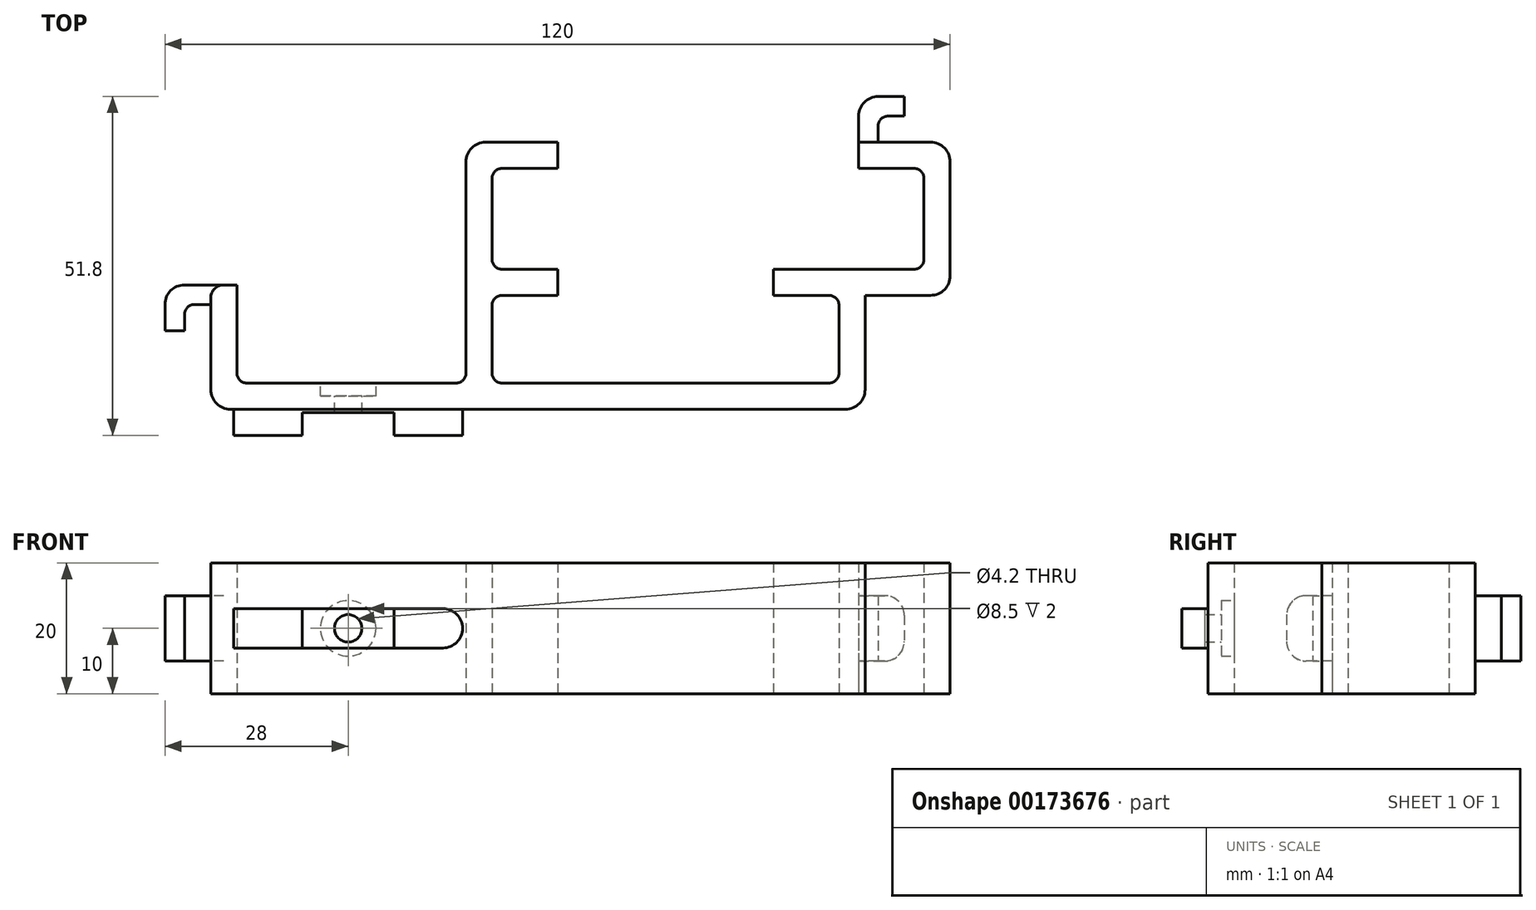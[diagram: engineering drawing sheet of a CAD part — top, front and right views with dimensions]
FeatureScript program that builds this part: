
annotation { "Feature Type Name" : "Feature", "Feature Type Description" : "" }
export const myFeature = defineFeature(function(context is Context, id is Id, definition is map)
    precondition{}
    {
        {
            var Q0;
            Q0=qCreatedBy(makeId("Top.planeOp"),FACE);
            var sketch = newSketch(context, id + "F0", { "sketchPlane" : qUnion([Q0])});
            skLineSegment(sketch, "E0", {"start": v(-35, 0) * mm, "end": v(0, 0) * mm});
            skLineSegment(sketch, "E1", {"start": v(0, 0) * mm, "end": v(0, 36.8) * mm});
            skLineSegment(sketch, "E2", {"start": v(0, 36.8) * mm, "end": v(14, 36.8) * mm});
            skLineSegment(sketch, "E3", {"start": v(14, 36.8) * mm, "end": v(14, 32.8) * mm});
            skLineSegment(sketch, "E4", {"start": v(14, 32.8) * mm, "end": v(4, 32.8) * mm});
            skLineSegment(sketch, "E5", {"start": v(4, 32.8) * mm, "end": v(4, 17.4) * mm});
            skLineSegment(sketch, "E6", {"start": v(4, 17.4) * mm, "end": v(14, 17.4) * mm});
            skLineSegment(sketch, "E7", {"start": v(14, 17.4) * mm, "end": v(14, 13.4) * mm});
            skLineSegment(sketch, "E8", {"start": v(14, 13.4) * mm, "end": v(4, 13.4) * mm});
            skLineSegment(sketch, "E9", {"start": v(4, 13.4) * mm, "end": v(4, 0) * mm});
            skLineSegment(sketch, "E10", {"start": v(4, 0) * mm, "end": v(57, 0) * mm});
            skLineSegment(sketch, "E11", {"start": v(57, 0) * mm, "end": v(57, 13.4) * mm});
            skLineSegment(sketch, "E12", {"start": v(57, 13.4) * mm, "end": v(47, 13.4) * mm});
            skLineSegment(sketch, "E13", {"start": v(47, 13.4) * mm, "end": v(47, 17.4) * mm});
            skLineSegment(sketch, "E14", {"start": v(47, 17.4) * mm, "end": v(70, 17.4) * mm});
            skLineSegment(sketch, "E15", {"start": v(70, 17.4) * mm, "end": v(70, 32.8) * mm});
            skLineSegment(sketch, "E16", {"start": v(70, 32.8) * mm, "end": v(60, 32.8) * mm});
            skLineSegment(sketch, "E17", {"start": v(60, 32.8) * mm, "end": v(60, 36.8) * mm});
            skLineSegment(sketch, "E18", {"start": v(60, 36.8) * mm, "end": v(74, 36.8) * mm});
            skLineSegment(sketch, "E19", {"start": v(74, 36.8) * mm, "end": v(74, 13.4) * mm});
            skLineSegment(sketch, "E20", {"start": v(74, 13.4) * mm, "end": v(61, 13.4) * mm});
            skLineSegment(sketch, "E21", {"start": v(61, 13.4) * mm, "end": v(61, -4) * mm});
            skLineSegment(sketch, "E22", {"start": v(61, -4) * mm, "end": v(-39, -4) * mm});
            skLineSegment(sketch, "E23", {"start": v(-39, -4) * mm, "end": v(-39, 15) * mm});
            skLineSegment(sketch, "E24", {"start": v(-39, 15) * mm, "end": v(-35, 15) * mm});
            skLineSegment(sketch, "E25", {"start": v(-35, 15) * mm, "end": v(-35, 0) * mm});
            skSolve(sketch);
        }
        {
            var Q0;
            Q0 = qSketchRegion(id + "F0", true);
            extrude(context, id + "F1", {"entities" : qUnion([Q0]), "endBound" : BoundingType.SYMMETRIC, "depth" : 20 * mm});
        }
        {
            var Q0;
            Q0=qCreatedBy(makeId("Top.planeOp"),FACE);
            var sketch = newSketch(context, id + "F2", { "sketchPlane" : qUnion([Q0])});
            skLineSegment(sketch, "E26.0", {"start": v(60, 36.8) * mm, "end": v(74, 36.8) * mm});
            skLineSegment(sketch, "E27.0", {"start": v(-39, -4) * mm, "end": v(-39, 15) * mm});
            skLineSegment(sketch, "E28", {"start": v(60, 36.8) * mm, "end": v(60, 43.8) * mm});
            skLineSegment(sketch, "E29", {"start": v(60, 43.8) * mm, "end": v(67, 43.8) * mm});
            skLineSegment(sketch, "E30", {"start": v(67, 43.8) * mm, "end": v(67, 40.8) * mm});
            skLineSegment(sketch, "E31", {"start": v(67, 40.8) * mm, "end": v(63, 40.8) * mm});
            skLineSegment(sketch, "E32", {"start": v(63, 40.8) * mm, "end": v(63, 36.8) * mm});
            skLineSegment(sketch, "E33", {"start": v(63, 36.8) * mm, "end": v(60, 36.8) * mm});
            skLineSegment(sketch, "E34", {"start": v(-39, 15) * mm, "end": v(-46, 15) * mm});
            skLineSegment(sketch, "E35", {"start": v(-46, 15) * mm, "end": v(-46, 8) * mm});
            skLineSegment(sketch, "E36", {"start": v(-46, 8) * mm, "end": v(-43, 8) * mm});
            skLineSegment(sketch, "E37", {"start": v(-43, 8) * mm, "end": v(-43, 12) * mm});
            skLineSegment(sketch, "E38", {"start": v(-43, 12) * mm, "end": v(-39, 12) * mm});
            skLineSegment(sketch, "E39", {"start": v(-39, 12) * mm, "end": v(-39, 15) * mm});
            skSolve(sketch);
        }
        {
            var Q0;
            Q0 = qSketchRegion(id + "F2", true);
            extrude(context, id + "F3", {"entities" : qUnion([Q0]), "operationType" : NewBodyOperationType.ADD, "endBound" : BoundingType.SYMMETRIC, "depth" : 10 * mm});
        }
        {
            var Q0;
            Q0=makeQuery(id+"F1.opExtrude","SWEPT_EDGE",EDGE,{"disambiguationData":[OSD([sQuery(id+"F0.wireOp",EDGE,"E0"),sQuery(id+"F0.wireOp",EDGE,"E25")])]});
            var Q1;
            Q1=makeQuery(id+"F1.opExtrude","SWEPT_EDGE",EDGE,{"disambiguationData":[OSD([sQuery(id+"F0.wireOp",EDGE,"E9"),sQuery(id+"F0.wireOp",EDGE,"E10")])]});
            var Q2;
            Q2=makeQuery(id+"F1.opExtrude","SWEPT_EDGE",EDGE,{"disambiguationData":[OSD([sQuery(id+"F0.wireOp",EDGE,"E5"),sQuery(id+"F0.wireOp",EDGE,"E6")])]});
            var Q3;
            Q3=makeQuery(id+"F3.opExtrude","SWEPT_EDGE",EDGE,{"disambiguationData":[OSD([sQuery(id+"F2.wireOp",EDGE,"E32"),sQuery(id+"F2.wireOp",EDGE,"E33")])]});
            var Q4;
            Q4=makeQuery(id+"F3.opExtrude","SWEPT_EDGE",EDGE,{"disambiguationData":[OSD([sQuery(id+"F2.wireOp",EDGE,"E31"),sQuery(id+"F2.wireOp",EDGE,"E32")])]});
            var Q5;
            Q5=makeQuery(id+"F1.opExtrude","SWEPT_EDGE",EDGE,{"disambiguationData":[OSD([sQuery(id+"F0.wireOp",EDGE,"E4"),sQuery(id+"F0.wireOp",EDGE,"E5")])]});
            var Q6;
            Q6=makeQuery(id+"F1.opExtrude","SWEPT_EDGE",EDGE,{"disambiguationData":[OSD([sQuery(id+"F0.wireOp",EDGE,"E8"),sQuery(id+"F0.wireOp",EDGE,"E9")])]});
            var Q7;
            Q7=makeQuery(id+"F1.opExtrude","SWEPT_EDGE",EDGE,{"disambiguationData":[OSD([sQuery(id+"F0.wireOp",EDGE,"E14"),sQuery(id+"F0.wireOp",EDGE,"E15")])]});
            var Q8;
            Q8=makeQuery(id+"F1.opExtrude","SWEPT_EDGE",EDGE,{"disambiguationData":[OSD([sQuery(id+"F0.wireOp",EDGE,"E10"),sQuery(id+"F0.wireOp",EDGE,"E11")])]});
            var Q9;
            Q9=makeQuery(id+"F1.opExtrude","SWEPT_EDGE",EDGE,{"disambiguationData":[OSD([sQuery(id+"F0.wireOp",EDGE,"E15"),sQuery(id+"F0.wireOp",EDGE,"E16")])]});
            var Q10;
            Q10=makeQuery(id+"F1.opExtrude","SWEPT_EDGE",EDGE,{"disambiguationData":[OSD([sQuery(id+"F0.wireOp",EDGE,"E11"),sQuery(id+"F0.wireOp",EDGE,"E12")])]});
            var Q11;
            Q11=makeQuery(id+"F3.opExtrude","SWEPT_EDGE",EDGE,{"disambiguationData":[OSD([sQuery(id+"F2.wireOp",EDGE,"E38"),sQuery(id+"F2.wireOp",EDGE,"E39")])]});
            var Q12;
            Q12=makeQuery(id+"F3.opExtrude","SWEPT_EDGE",EDGE,{"disambiguationData":[OSD([sQuery(id+"F2.wireOp",EDGE,"E37"),sQuery(id+"F2.wireOp",EDGE,"E38")])]});
            var Q13;
            Q13=makeQuery(id+"F1.opExtrude","SWEPT_EDGE",EDGE,{"disambiguationData":[OSD([sQuery(id+"F0.wireOp",EDGE,"E0"),sQuery(id+"F0.wireOp",EDGE,"E1")])]});
            fillet(context, id + "F4", {"entities" : qUnion([Q0, Q1, Q2, Q3, Q4, Q5, Q6, Q7, Q8, Q9, Q10, Q11, Q12, Q13]), "radius" : 1.5 * mm, "allowEdgeOverflow" : false});
        }
        {
            var Q0;
            Q0=makeQuery(id+"F1.opExtrude","SWEPT_EDGE",EDGE,{"disambiguationData":[OSD([sQuery(id+"F0.wireOp",EDGE,"E22"),sQuery(id+"F0.wireOp",EDGE,"E23")])]});
            var Q1;
            Q1=makeQuery(id+"F1.opExtrude","SWEPT_EDGE",EDGE,{"disambiguationData":[OSD([sQuery(id+"F0.wireOp",EDGE,"E21"),sQuery(id+"F0.wireOp",EDGE,"E22")])]});
            var Q2;
            Q2=makeQuery(id+"F1.opExtrude","SWEPT_EDGE",EDGE,{"disambiguationData":[OSD([sQuery(id+"F0.wireOp",EDGE,"E19"),sQuery(id+"F0.wireOp",EDGE,"E20")])]});
            var Q3;
            Q3=makeQuery(id+"F1.opExtrude","SWEPT_EDGE",EDGE,{"disambiguationData":[OSD([sQuery(id+"F0.wireOp",EDGE,"E18"),sQuery(id+"F0.wireOp",EDGE,"E19")])]});
            var Q4;
            Q4=makeQuery(id+"F3.opExtrude","SWEPT_EDGE",EDGE,{"disambiguationData":[OSD([sQuery(id+"F2.wireOp",EDGE,"E28"),sQuery(id+"F2.wireOp",EDGE,"E29")])]});
            var Q5;
            Q5=makeQuery(id+"F3.opExtrude","SWEPT_EDGE",EDGE,{"disambiguationData":[OSD([sQuery(id+"F2.wireOp",EDGE,"E34"),sQuery(id+"F2.wireOp",EDGE,"E35")])]});
            var Q6;
            Q6=makeQuery(id+"F1.opExtrude","SWEPT_EDGE",EDGE,{"disambiguationData":[OSD([sQuery(id+"F0.wireOp",EDGE,"E1"),sQuery(id+"F0.wireOp",EDGE,"E2")])]});
            var Q7;
            Q7=makeQuery(id+"F3.opExtrude","CAP_EDGE",EDGE,{"disambiguationData":[OSD([sQuery(id+"F2.wireOp",EDGE,"E36")])],"isStart":false});
            var Q8;
            Q8=makeQuery(id+"F3.opExtrude","CAP_EDGE",EDGE,{"disambiguationData":[OSD([sQuery(id+"F2.wireOp",EDGE,"E30")])],"isStart":false});
            var Q9;
            Q9=makeQuery(id+"F3.opExtrude","CAP_EDGE",EDGE,{"disambiguationData":[OSD([sQuery(id+"F2.wireOp",EDGE,"E36")])],"isStart":true});
            var Q10;
            Q10=makeQuery(id+"F3.opExtrude","CAP_EDGE",EDGE,{"disambiguationData":[OSD([sQuery(id+"F2.wireOp",EDGE,"E30")])],"isStart":true});
            fillet(context, id + "F5", {"entities" : qUnion([Q0, Q1, Q2, Q3, Q4, Q5, Q6, Q7, Q8, Q9, Q10]), "radius" : 3 * mm, "tangentPropagation" : true, "allowEdgeOverflow" : false});
        }
        {
            var Q0;
            Q0=qCreatedBy(makeId("Top.planeOp"),FACE);
            var sketch = newSketch(context, id + "F6", { "sketchPlane" : qUnion([Q0])});
            skLineSegment(sketch, "E40", {"start": v(-0.5, -8) * mm, "end": v(-11, -8) * mm});
            skLineSegment(sketch, "E41", {"start": v(-11, -8) * mm, "end": v(-11, -4.5) * mm});
            skLineSegment(sketch, "E42", {"start": v(-11, -4.5) * mm, "end": v(-25, -4.5) * mm});
            skLineSegment(sketch, "E43", {"start": v(-25, -4.5) * mm, "end": v(-25, -8) * mm});
            skLineSegment(sketch, "E44", {"start": v(-25, -8) * mm, "end": v(-35.5, -8) * mm});
            skLineSegment(sketch, "E45.0", {"start": v(58, -4) * mm, "end": v(-36, -4) * mm});
            skLineSegment(sketch, "E46", {"start": v(-35.5, -8) * mm, "end": v(-35.5, -4) * mm});
            skLineSegment(sketch, "E47", {"start": v(-35.5, -4) * mm, "end": v(-0.5, -4) * mm});
            skLineSegment(sketch, "E48", {"start": v(-0.5, -4) * mm, "end": v(-0.5, -8) * mm});
            skPoint(sketch, "E49", {"position": v(-18, -4.5) * mm});
            skSolve(sketch);
        }
        {
            var Q0;
            Q0 = qSketchRegion(id + "F6", true);
            extrude(context, id + "F7", {"entities" : qUnion([Q0]), "operationType" : NewBodyOperationType.ADD, "endBound" : BoundingType.SYMMETRIC, "depth" : 6 * mm});
        }
        {
            var Q0;
            Q0=qCreatedBy(makeId("Top.planeOp"),FACE);
            var sketch = newSketch(context, id + "F8", { "sketchPlane" : qUnion([Q0])});
            skPoint(sketch, "E50.0", {"position": v(-18, -4.5) * mm});
            skLineSegment(sketch, "E51", {"start": v(-18, -4.5) * mm, "end": v(-18, 8) * mm, "construction": true});
            skLineSegment(sketch, "E52.0", {"start": v(-11, -4.5) * mm, "end": v(-25, -4.5) * mm});
            skLineSegment(sketch, "E53.0", {"start": v(-33.5, 0) * mm, "end": v(-1.5, 0) * mm});
            skLineSegment(sketch, "E54", {"start": v(-18, -4.5) * mm, "end": v(-15.9, -4.5) * mm});
            skLineSegment(sketch, "E55", {"start": v(-15.9, -4.5) * mm, "end": v(-15.9, -2) * mm});
            skLineSegment(sketch, "E56", {"start": v(-15.9, -2) * mm, "end": v(-13.75, -2) * mm});
            skLineSegment(sketch, "E57", {"start": v(-13.75, -2) * mm, "end": v(-13.75, 0) * mm});
            skLineSegment(sketch, "E58", {"start": v(-13.75, 0) * mm, "end": v(-18, 0) * mm});
            skLineSegment(sketch, "E59", {"start": v(-18, 0) * mm, "end": v(-18, -4.5) * mm});
            skSolve(sketch);
        }
        {
            var Q0;
            Q0 = qSketchRegion(id + "F8", true);
            var Q1;
            Q1=sQuery(id+"F8.wireOp",EDGE,"E51");
            revolve(context, id + "F9", {"operationType" : NewBodyOperationType.REMOVE, "entities" : qUnion([Q0]), "axis" : qUnion([Q1]), "revolveType" : RevolveType.FULL, "oppositeDirection" : true});
        }
        {
            var Q0;
            {var subQ0=sQuery(id+"F0.wireOp",EDGE,"E24");var subQ1=sQuery(id+"F0.wireOp",EDGE,"E23");var subQ2=sQuery(id+"F2.wireOp",EDGE,"E34");Q0=makeQuery(id+"F3.boolean.opBoolean","SPLIT",EDGE,{"disambiguationData":[TD([makeQuery(id+"F3.opExtrude","CAP_FACE",FACE,{"disambiguationData":[OSD([subQ2,sQuery(id+"F2.wireOp",EDGE,"E35"),sQuery(id+"F2.wireOp",EDGE,"E36"),sQuery(id+"F2.wireOp",EDGE,"E37"),sQuery(id+"F2.wireOp",EDGE,"E38"),sQuery(id+"F2.wireOp",EDGE,"E39")])],"isStart":true})])],"derivedFrom":makeQuery(id+"F1.opExtrude","SWEPT_EDGE",EDGE,{"disambiguationData":[OSD([subQ1,subQ0])]})});}
            var Q1;
            {var subQ0=sQuery(id+"F2.wireOp",EDGE,"E34");var subQ1=sQuery(id+"F0.wireOp",EDGE,"E24");var subQ2=sQuery(id+"F0.wireOp",EDGE,"E23");Q1=makeQuery(id+"F3.boolean.opBoolean","SPLIT",EDGE,{"disambiguationData":[TD([makeQuery(id+"F3.opExtrude","CAP_FACE",FACE,{"disambiguationData":[OSD([subQ0,sQuery(id+"F2.wireOp",EDGE,"E35"),sQuery(id+"F2.wireOp",EDGE,"E36"),sQuery(id+"F2.wireOp",EDGE,"E37"),sQuery(id+"F2.wireOp",EDGE,"E38"),sQuery(id+"F2.wireOp",EDGE,"E39")])],"isStart":false})])],"derivedFrom":makeQuery(id+"F1.opExtrude","SWEPT_EDGE",EDGE,{"disambiguationData":[OSD([subQ2,subQ1])]})});}
            fillet(context, id + "F10", {"entities" : qUnion([Q0, Q1]), "radius" : 2 * mm, "tangentPropagation" : true, "allowEdgeOverflow" : false});
        }
        {
            var Q0;
            Q0=makeQuery(id+"F7.opExtrude","CAP_EDGE",EDGE,{"disambiguationData":[OSD([sQuery(id+"F6.wireOp",EDGE,"E48")])],"isStart":true});
            var Q1;
            Q1=makeQuery(id+"F7.opExtrude","CAP_EDGE",EDGE,{"disambiguationData":[OSD([sQuery(id+"F6.wireOp",EDGE,"E48")])],"isStart":false});
            fillet(context, id + "F11", {"entities" : qUnion([Q0, Q1]), "radius" : 3 * mm, "tangentPropagation" : true, "allowEdgeOverflow" : false});
        }
    });
